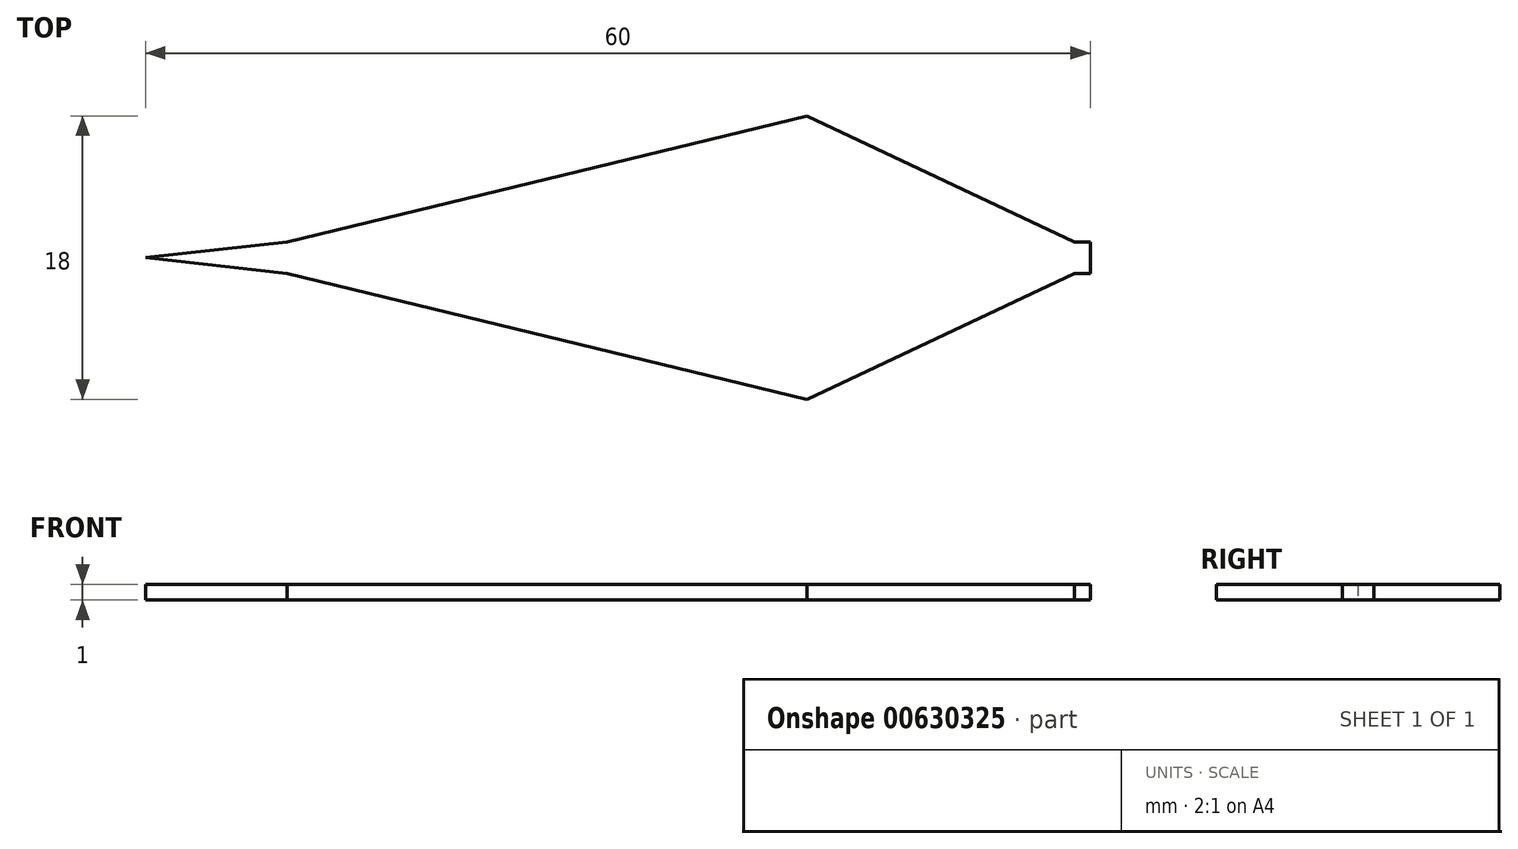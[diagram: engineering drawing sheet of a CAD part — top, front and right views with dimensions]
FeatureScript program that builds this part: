
annotation { "Feature Type Name" : "Feature", "Feature Type Description" : "" }
export const myFeature = defineFeature(function(context is Context, id is Id, definition is map)
    precondition{}
    {
        {
            var Q0;
            Q0=qCreatedBy(makeId("Top.planeOp"),FACE);
            var sketch = newSketch(context, id + "F0", { "sketchPlane" : qUnion([Q0])});
            skLineSegment(sketch, "E0.bottom", {"start": v(-25.5, 0) * mm, "end": v(25.5, 0) * mm});
            skLineSegment(sketch, "E0.top", {"start": v(-25.5, 1) * mm, "end": v(25.5, 1) * mm});
            skLineSegment(sketch, "E0.left", {"start": v(-25.5, 0) * mm, "end": v(-25.5, 1) * mm});
            skLineSegment(sketch, "E0.right", {"start": v(25.5, 0) * mm, "end": v(25.5, 1) * mm});
            skLineSegment(sketch, "E1", {"start": v(-25.5, 0) * mm, "end": v(-25.5, -1) * mm});
            skLineSegment(sketch, "E2", {"start": v(-25.5, -1) * mm, "end": v(25.5, -1) * mm});
            skLineSegment(sketch, "E3", {"start": v(25.5, -1) * mm, "end": v(25.5, 0) * mm});
            skLineSegment(sketch, "E4", {"start": v(-25.5, -1) * mm, "end": v(-25.5, -3) * mm, "construction": true});
            skLineSegment(sketch, "E5", {"start": v(-25.5, -3) * mm, "end": v(25.5, -3) * mm, "construction": true});
            skLineSegment(sketch, "E6", {"start": v(25.5, -3) * mm, "end": v(25.5, -1) * mm, "construction": true});
            skLineSegment(sketch, "E7", {"start": v(-25.5, 3) * mm, "end": v(25.5, 3) * mm, "construction": true});
            skLineSegment(sketch, "E8", {"start": v(-25.5, 3) * mm, "end": v(-25.5, 1) * mm, "construction": true});
            skLineSegment(sketch, "E9", {"start": v(25.5, 3) * mm, "end": v(25.5, 1) * mm, "construction": true});
            skLineSegment(sketch, "E10", {"start": v(-16.5, 3) * mm, "end": v(-16.5, -3) * mm, "construction": true});
            skLineSegment(sketch, "E11", {"start": v(-16.5, 3.06) * mm, "end": v(-16.5, 7.6) * mm, "construction": true});
            skLineSegment(sketch, "E12", {"start": v(-25.5, 2.93) * mm, "end": v(-25.5, 7.6) * mm, "construction": true});
            skLineSegment(sketch, "E13", {"start": v(-25.5, 7.6) * mm, "end": v(-16.5, 7.6) * mm});
            skLineSegment(sketch, "E14", {"start": v(-16.5, 7.6) * mm, "end": v(-4.5, 7.6) * mm});
            skLineSegment(sketch, "E15", {"start": v(-4.5, 7.6) * mm, "end": v(7.5, 7.6) * mm, "construction": true});
            skLineSegment(sketch, "E16", {"start": v(7.5, 7.6) * mm, "end": v(16.5, 7.6) * mm, "construction": true});
            skLineSegment(sketch, "E17", {"start": v(16.5, 7.6) * mm, "end": v(25.5, 7.6) * mm, "construction": true});
            skLineSegment(sketch, "E18", {"start": v(25.5, 3) * mm, "end": v(25.5, 7.6) * mm, "construction": true});
            skLineSegment(sketch, "E19", {"start": v(7.5, 9) * mm, "end": v(7.5, 3) * mm, "construction": true});
            skLineSegment(sketch, "E20", {"start": v(-25.5, 1) * mm, "end": v(7.5, 9) * mm});
            skLineSegment(sketch, "E21", {"start": v(7.5, -3) * mm, "end": v(7.5, 3) * mm, "construction": true});
            skLineSegment(sketch, "E22", {"start": v(7.5, -3) * mm, "end": v(7.5, -9) * mm, "construction": true});
            skLineSegment(sketch, "E23", {"start": v(-25.5, -1) * mm, "end": v(7.5, -9) * mm});
            skLineSegment(sketch, "E24", {"start": v(24.5, 3) * mm, "end": v(24.5, -3) * mm, "construction": true});
            skLineSegment(sketch, "E25", {"start": v(24.5, -3) * mm, "end": v(24.5, -4.27) * mm});
            skLineSegment(sketch, "E26", {"start": v(25.5, -3) * mm, "end": v(25.5, -4.27) * mm});
            skLineSegment(sketch, "E27", {"start": v(24.5, -4.27) * mm, "end": v(25.5, -4.27) * mm});
            skLineSegment(sketch, "E28", {"start": v(7.5, 9) * mm, "end": v(24.5, 1) * mm});
            skLineSegment(sketch, "E29", {"start": v(7.5, -9) * mm, "end": v(24.5, -1) * mm});
            skLineSegment(sketch, "E30", {"start": v(-25.5, 0) * mm, "end": v(-34.5, 0) * mm});
            skLineSegment(sketch, "E31", {"start": v(-34.5, 0) * mm, "end": v(-25.5, 1) * mm});
            skLineSegment(sketch, "E32", {"start": v(-34.5, 0) * mm, "end": v(-25.5, -1) * mm});
            skLineSegment(sketch, "E33", {"start": v(-15.83, 0) * mm, "end": v(-15.83, 2.5) * mm});
            skFitSpline(sketch, "E34", {"points": [v(-25.5, 1) * mm, v(7.5, 3) * mm], "startDerivative": vector(33, 7.14) * mm, "endDerivative": vector(62.12, 1.5) * mm});
            skFitSpline(sketch, "E35.MirrorCS", {"points": [v(-25.5, -1) * mm, v(7.5, -3) * mm], "startDerivative": vector(33, -7.14) * mm, "endDerivative": vector(62.12, -1.5) * mm});
            skFitSpline(sketch, "E36", {"points": [v(7.5, 3) * mm, v(24.5, 1) * mm], "startDerivative": vector(19.89, -1.31) * mm, "endDerivative": vector(17.03, -2.93) * mm});
            skFitSpline(sketch, "E37.MirrorCS", {"points": [v(7.5, -3) * mm, v(24.5, -1) * mm], "startDerivative": vector(19.89, 1.31) * mm, "endDerivative": vector(17.03, 2.93) * mm});
            skSolve(sketch);
        }
        {
            var Q0;
            Q0 = qSketchRegion(id + "F0", true);
            var Q1;
            Q1 = qSketchRegion(id + "F7zgZvhvTiggVxQ_0", true);
            extrude(context, id + "F1", {"entities" : qUnion([Q0, Q1]), "depth" : 1 * mm, "offsetDistance" : 25 * mm});
        }
    });
